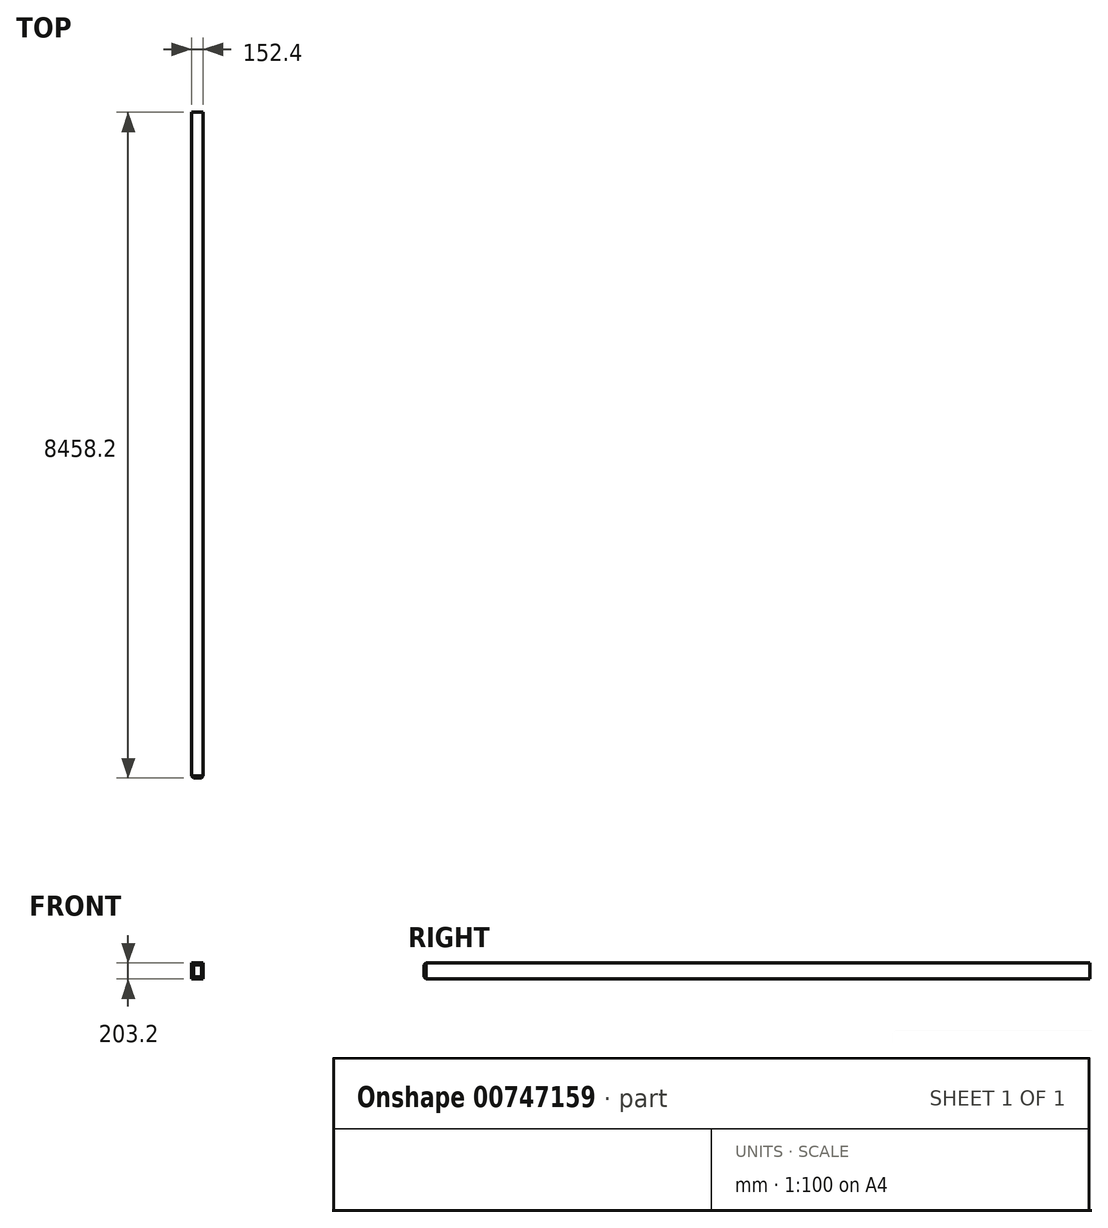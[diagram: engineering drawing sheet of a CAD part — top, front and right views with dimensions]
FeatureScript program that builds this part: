
annotation { "Feature Type Name" : "Feature", "Feature Type Description" : "" }
export const myFeature = defineFeature(function(context is Context, id is Id, definition is map)
    precondition{}
    {
        {
            var Q0;
            Q0=qCreatedBy(makeId("Front.planeOp"),FACE);
            var sketch = newSketch(context, id + "F0", { "sketchPlane" : qUnion([Q0])});
            skLineSegment(sketch, "E0.bottom", {"start": v(-253.42, 0) * mm, "end": v(-101.02, 0) * mm});
            skLineSegment(sketch, "E0.top", {"start": v(-253.42, -203.2) * mm, "end": v(-101.02, -203.2) * mm});
            skLineSegment(sketch, "E0.left", {"start": v(-253.42, 0) * mm, "end": v(-253.42, -203.2) * mm});
            skLineSegment(sketch, "E0.right", {"start": v(-101.02, 0) * mm, "end": v(-101.02, -203.2) * mm});
            skSolve(sketch);
        }
        {
            var Q0;
            Q0 = qSketchRegion(id + "F0", true);
            extrude(context, id + "F1", {"entities" : qUnion([Q0]), "depth" : 8458.2 * mm, "offsetDistance" : 25.4 * mm});
        }
        {
            var Q0;
            Q0=makeQuery(id+"F1.opExtrude","CAP_EDGE",EDGE,{"disambiguationData":[OSD([sQuery(id+"F0.wireOp",EDGE,"E0.bottom")])],"isStart":false});
            var Q1;
            Q1=makeQuery(id+"F1.opExtrude","CAP_EDGE",EDGE,{"disambiguationData":[OSD([sQuery(id+"F0.wireOp",EDGE,"E0.left")])],"isStart":false});
            var Q2;
            Q2=makeQuery(id+"F1.opExtrude","CAP_EDGE",EDGE,{"disambiguationData":[OSD([sQuery(id+"F0.wireOp",EDGE,"E0.top")])],"isStart":false});
            var Q3;
            Q3=makeQuery(id+"F1.opExtrude","CAP_EDGE",EDGE,{"disambiguationData":[OSD([sQuery(id+"F0.wireOp",EDGE,"E0.right")])],"isStart":false});
            chamfer(context, id + "F2", {"entities" : qUnion([Q0, Q1, Q2, Q3]), "width" : 25.4 * mm, "tangentPropagation" : true});
        }
    });
